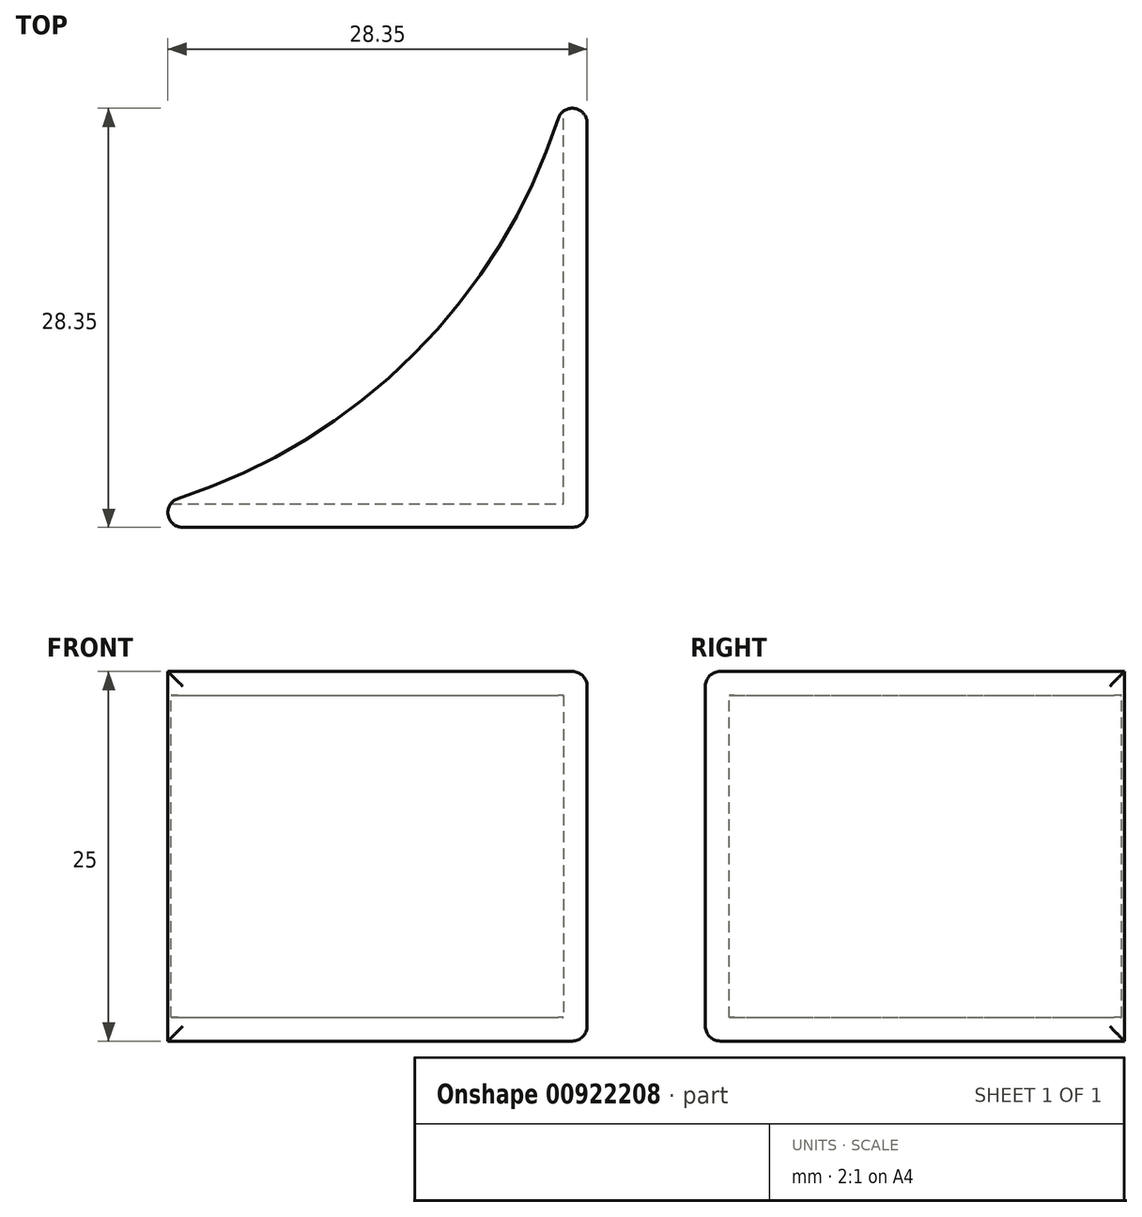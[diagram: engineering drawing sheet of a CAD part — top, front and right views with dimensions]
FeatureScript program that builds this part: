
annotation { "Feature Type Name" : "Feature", "Feature Type Description" : "" }
export const myFeature = defineFeature(function(context is Context, id is Id, definition is map)
    precondition{}
    {
        {
            var Q0;
            Q0=qCreatedBy(makeId("Top.planeOp"),FACE);
            var sketch = newSketch(context, id + "F0", { "sketchPlane" : qUnion([Q0])});
            skCircle(sketch, "E0.cCircle", {"center": v(0, 0) * mm, "radius": 20 * mm, "construction": true});
            skLineSegment(sketch, "E0.0", {"start": v(20, 20) * mm, "end": v(20, -20) * mm});
            skLineSegment(sketch, "E0.1", {"start": v(20, -20) * mm, "end": v(-20, -20) * mm});
            skLineSegment(sketch, "E0.2", {"start": v(-20, -20) * mm, "end": v(-20, 20) * mm});
            skLineSegment(sketch, "E0.3", {"start": v(-20, 20) * mm, "end": v(20, 20) * mm});
            skPoint(sketch, "E0.0.midPoint", {"position": v(20, 0) * mm});
            skSolve(sketch);
        }
        {
            var Q0;
            Q0 = qSketchRegion(id + "F0", true);
            extrude(context, id + "F1", {"entities" : qUnion([Q0]), "depth" : 25 * mm, "offsetDistance" : 25 * mm});
        }
        {
            var Q0;
            Q0=makeQuery(id+"F1.opExtrude","SWEPT_FACE",FACE,{"disambiguationData":[OSD([sQuery(id+"F0.wireOp",EDGE,"E0.3")])]});
            var sketch = newSketch(context, id + "F2", { "sketchPlane" : qUnion([Q0])});
            skPoint(sketch, "E1", {"position": v(20, 23.4) * mm});
            skPoint(sketch, "E2", {"position": v(20, 1.6) * mm});
            skPoint(sketch, "E3", {"position": v(-18.4, 23.4) * mm});
            skPoint(sketch, "E4", {"position": v(-18.4, 1.6) * mm});
            skLineSegment(sketch, "E5.bottom", {"start": v(20, 23.4) * mm, "end": v(-18.4, 23.4) * mm});
            skLineSegment(sketch, "E5.top", {"start": v(20, 1.6) * mm, "end": v(-18.4, 1.6) * mm});
            skLineSegment(sketch, "E5.left", {"start": v(20, 23.4) * mm, "end": v(20, 1.6) * mm});
            skLineSegment(sketch, "E5.right", {"start": v(-18.4, 23.4) * mm, "end": v(-18.4, 1.6) * mm});
            skSolve(sketch);
        }
        {
            var Q0;
            Q0=makeQuery(id+"F2.imprint","IMPRINT",FACE,{"disambiguationData":[TD([[makeQuery(id+"F2.imprint","IMPRINT",EDGE,{"derivedFrom":sQuery(id+"F2.wireOp",EDGE,"E5.bottom")}),1.0]])]});
            extrude(context, id + "F3", {"entities" : qUnion([Q0]), "operationType" : NewBodyOperationType.REMOVE, "oppositeDirection" : true, "depth" : 38.4 * mm, "offsetDistance" : 25 * mm});
        }
        {
            var Q0;
            Q0=makeQuery(id+"F1.opExtrude","CAP_FACE",FACE,{"disambiguationData":[OSD([sQuery(id+"F0.wireOp",EDGE,"E0.0"),sQuery(id+"F0.wireOp",EDGE,"E0.1"),sQuery(id+"F0.wireOp",EDGE,"E0.2"),sQuery(id+"F0.wireOp",EDGE,"E0.3")])],"isStart":false});
            var sketch = newSketch(context, id + "F4", { "sketchPlane" : qUnion([Q0])});
            skCircle(sketch, "E6", {"center": v(-20, 20) * mm, "radius": 40 * mm});
            skSolve(sketch);
        }
        {
            var Q0;
            {var subQ2=makeQuery(id+"F1.opExtrude","CAP_EDGE",EDGE,{"disambiguationData":[OSD([sQuery(id+"F0.wireOp",EDGE,"E0.2")])],"isStart":false});Q0=makeQuery(id+"F4.imprint","IMPRINT",FACE,{"disambiguationData":[TD([[makeQuery(id+"F4.imprint","IMPRINT",EDGE,{"derivedFrom":subQ2}),-1.0]])]});}
            extrude(context, id + "F5", {"entities" : qUnion([Q0]), "operationType" : NewBodyOperationType.REMOVE, "oppositeDirection" : true, "depth" : 25 * mm, "offsetDistance" : 25 * mm});
        }
        {
            var Q0;
            {var subQ0=sQuery(id+"F0.wireOp",EDGE,"E0.3");var subQ1=sQuery(id+"F0.wireOp",EDGE,"E0.0");Q0=makeQuery(id+"F5.boolean.opBoolean","MERGE",EDGE,{"derivedFrom":[makeQuery(id+"F1.opExtrude","SWEPT_EDGE",EDGE,{"disambiguationData":[OSD([subQ1,subQ0])]})],"fromTools":[makeQuery(id+"F5.opExtrude","SWEPT_EDGE",EDGE,{"disambiguationData":[OSD([subQ1,subQ0,sQuery(id+"F4.wireOp",EDGE,"E6")])]})]});}
            var Q1;
            {var subQ0=sQuery(id+"F0.wireOp",EDGE,"E0.2");var subQ1=sQuery(id+"F0.wireOp",EDGE,"E0.1");Q1=makeQuery(id+"F5.boolean.opBoolean","MERGE",EDGE,{"derivedFrom":[makeQuery(id+"F1.opExtrude","SWEPT_EDGE",EDGE,{"disambiguationData":[OSD([subQ1,subQ0])]})],"fromTools":[makeQuery(id+"F5.opExtrude","SWEPT_EDGE",EDGE,{"disambiguationData":[OSD([subQ1,subQ0,sQuery(id+"F4.wireOp",EDGE,"E6")])]})]});}
            var Q2;
            Q2=makeQuery(id+"F1.opExtrude","SWEPT_EDGE",EDGE,{"disambiguationData":[OSD([sQuery(id+"F0.wireOp",EDGE,"E0.0"),sQuery(id+"F0.wireOp",EDGE,"E0.1")])]});
            var Q3;
            Q3=makeQuery(id+"F1.opExtrude","CAP_EDGE",EDGE,{"disambiguationData":[OSD([sQuery(id+"F0.wireOp",EDGE,"E0.1")])],"isStart":true});
            var Q4;
            Q4=makeQuery(id+"F1.opExtrude","CAP_EDGE",EDGE,{"disambiguationData":[OSD([sQuery(id+"F0.wireOp",EDGE,"E0.0")])],"isStart":true});
            var Q5;
            Q5=makeQuery(id+"F1.opExtrude","CAP_EDGE",EDGE,{"disambiguationData":[OSD([sQuery(id+"F0.wireOp",EDGE,"E0.0")])],"isStart":false});
            var Q6;
            Q6=makeQuery(id+"F1.opExtrude","CAP_EDGE",EDGE,{"disambiguationData":[OSD([sQuery(id+"F0.wireOp",EDGE,"E0.1")])],"isStart":false});
            fillet(context, id + "F6", {"entities" : qUnion([Q0, Q1, Q2, Q3, Q4, Q5, Q6]), "radius" : 1 * mm, "tangentPropagation" : true, "allowEdgeOverflow" : false});
        }
    });
